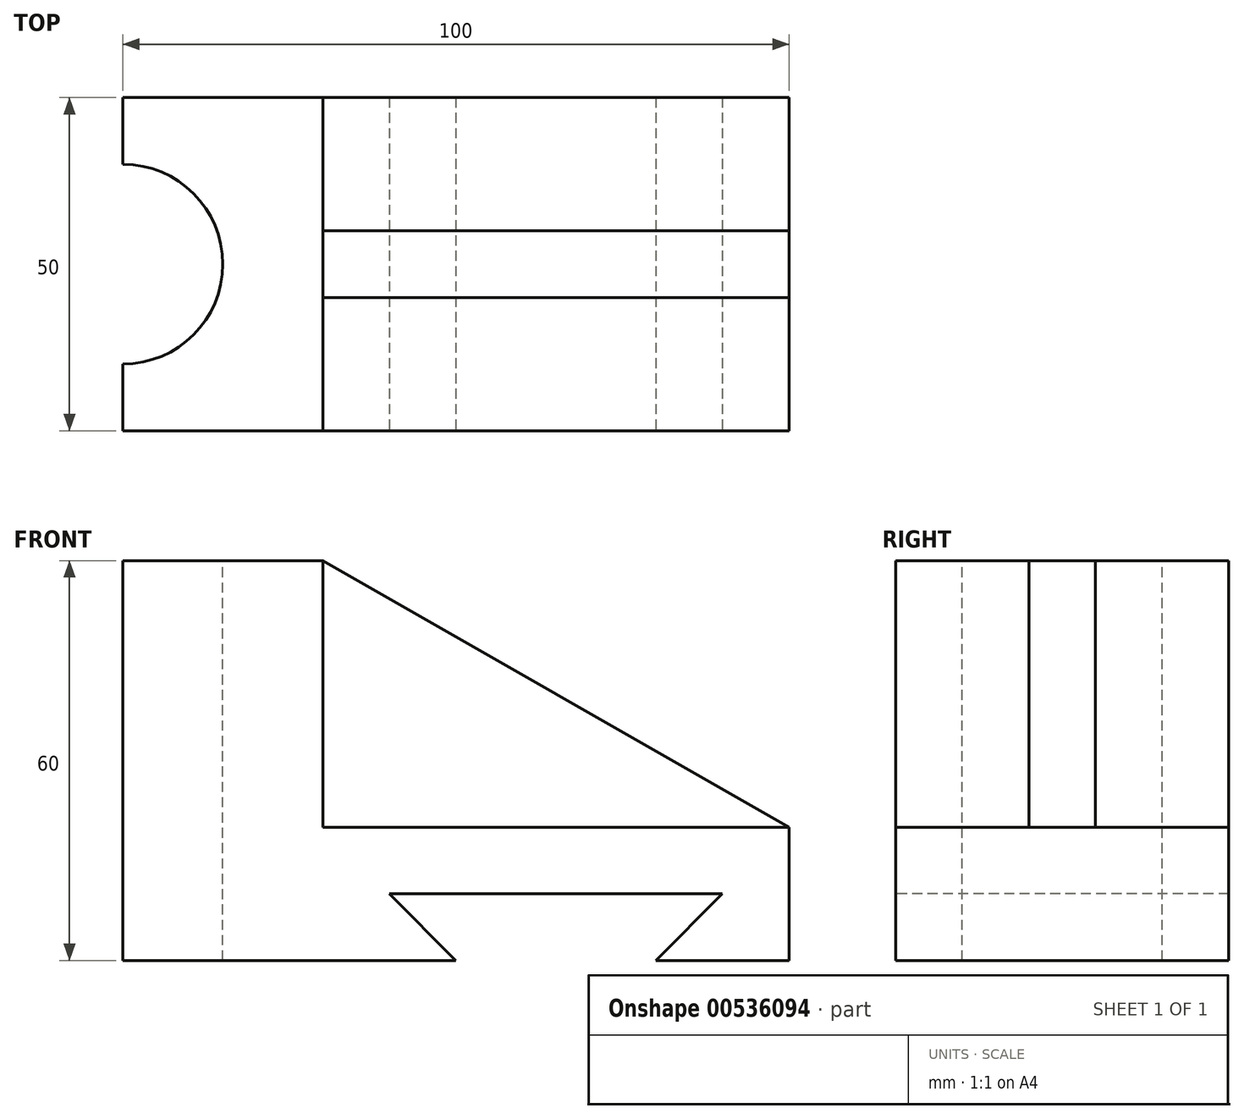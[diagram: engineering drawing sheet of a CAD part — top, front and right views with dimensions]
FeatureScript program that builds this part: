
annotation { "Feature Type Name" : "Feature", "Feature Type Description" : "" }
export const myFeature = defineFeature(function(context is Context, id is Id, definition is map)
    precondition{}
    {
        {
            var Q0;
            Q0=qCreatedBy(makeId("Top.planeOp"),FACE);
            var sketch = newSketch(context, id + "F0", { "sketchPlane" : qUnion([Q0])});
            skLineSegment(sketch, "E0.bottom", {"start": v(50, 25) * mm, "end": v(-50, 25) * mm});
            skLineSegment(sketch, "E0.top", {"start": v(50, -25) * mm, "end": v(-50, -25) * mm});
            skLineSegment(sketch, "E0.left", {"start": v(50, 25) * mm, "end": v(50, -25) * mm});
            skLineSegment(sketch, "E0.right", {"start": v(-50, 25) * mm, "end": v(-50, -25) * mm});
            skPoint(sketch, "E0.middle", {"position": v(0, 0) * mm});
            skLineSegment(sketch, "E1", {"start": v(-50, 25) * mm, "end": v(-20, 25) * mm});
            skLineSegment(sketch, "E2", {"start": v(-20, 25) * mm, "end": v(-20, -25) * mm});
            skLineSegment(sketch, "E3", {"start": v(-20, -25) * mm, "end": v(-50, -25) * mm});
            skSolve(sketch);
        }
        {
            var Q0;
            Q0=makeQuery(id+"F0.imprint","IMPRINT",FACE,{"disambiguationData":[TD([[makeQuery(id+"F0.imprint","IMPRINT",EDGE,{"derivedFrom":sQuery(id+"F0.wireOp",EDGE,"E0.right")}),1.0]])]});
            extrude(context, id + "F1", {"entities" : qUnion([Q0]), "depth" : 60 * mm, "offsetDistance" : 25 * mm});
        }
        {
            var Q0;
            Q0=makeQuery(id+"F0.imprint","IMPRINT",FACE,{"disambiguationData":[TD([[makeQuery(id+"F0.imprint","IMPRINT",EDGE,{"derivedFrom":sQuery(id+"F0.wireOp",EDGE,"E0.bottom")}),1.0]])]});
            extrude(context, id + "F2", {"entities" : qUnion([Q0]), "operationType" : NewBodyOperationType.ADD, "depth" : 20 * mm, "offsetDistance" : 25 * mm});
        }
        {
            var Q0;
            Q0=makeQuery(id+"F1.opExtrude","CAP_FACE",FACE,{"disambiguationData":[OSD([sQuery(id+"F0.wireOp",EDGE,"E0.right"),sQuery(id+"F0.wireOp",EDGE,"E1"),sQuery(id+"F0.wireOp",EDGE,"E2"),sQuery(id+"F0.wireOp",EDGE,"E3")])],"isStart":false});
            var sketch = newSketch(context, id + "F3", { "sketchPlane" : qUnion([Q0])});
            skPoint(sketch, "E4", {"position": v(-50, 15) * mm});
            skPoint(sketch, "E5", {"position": v(-50, -15) * mm});
            skCircle(sketch, "E6", {"center": v(-50, 0) * mm, "radius": 15 * mm});
            skSolve(sketch);
        }
        {
            var Q0;
            {var subQ0=sQuery(id+"F3.wireOp",EDGE,"E6");var subQ1=makeQuery(id+"F1.opExtrude","CAP_EDGE",EDGE,{"disambiguationData":[OSD([sQuery(id+"F0.wireOp",EDGE,"E0.right")])],"isStart":false});var subQ2=makeQuery(id+"F3.imprint","INTERSECT",VERTEX,{"disambiguationData":[OD(0.0)],"derivedFrom":[subQ1,subQ0]});Q0=makeQuery(id+"F3.imprint","IMPRINT",FACE,{"disambiguationData":[TD([[makeQuery(id+"F3.imprint","IMPRINT",EDGE,{"disambiguationData":[TD([[subQ2,1.0]])],"derivedFrom":subQ0}),1.0]])]});}
            extrude(context, id + "F4", {"entities" : qUnion([Q0]), "operationType" : NewBodyOperationType.REMOVE, "oppositeDirection" : true, "depth" : 71.1 * mm, "offsetDistance" : 25 * mm});
        }
        {
            var Q0;
            Q0=qCreatedBy(makeId("Front.planeOp"),FACE);
            var sketch = newSketch(context, id + "F5", { "sketchPlane" : qUnion([Q0])});
            skLineSegment(sketch, "E7.0.0", {"start": v(-50, 0) * mm, "end": v(50, 0) * mm});
            skLineSegment(sketch, "E7.0.1", {"start": v(50, 0) * mm, "end": v(50, 20) * mm});
            skLineSegment(sketch, "E7.0.2", {"start": v(50, 20) * mm, "end": v(-20, 20) * mm});
            skLineSegment(sketch, "E7.0.3", {"start": v(-20, 20) * mm, "end": v(-20, 60) * mm});
            skLineSegment(sketch, "E7.0.4", {"start": v(-20, 60) * mm, "end": v(-50, 60) * mm});
            skLineSegment(sketch, "E7.0.5", {"start": v(-50, 60) * mm, "end": v(-50, 0) * mm});
            skLineSegment(sketch, "E8", {"start": v(-20, 60) * mm, "end": v(50, 20) * mm});
            skSolve(sketch);
        }
        {
            var Q0;
            Q0=makeQuery(id+"F5.imprint","IMPRINT",FACE,{"disambiguationData":[TD([[makeQuery(id+"F5.imprint","IMPRINT",EDGE,{"derivedFrom":sQuery(id+"F5.wireOp",EDGE,"E7.0.2")}),-1.0]])]});
            extrude(context, id + "F6", {"entities" : qUnion([Q0]), "operationType" : NewBodyOperationType.ADD, "depth" : 5 * mm, "offsetDistance" : 25 * mm, "hasSecondDirection" : true, "secondDirectionOppositeDirection" : true, "secondDirectionDepth" : 5 * mm});
        }
        {
            var Q0;
            Q0=makeQuery(id+"F2.boolean.opBoolean","MERGE",FACE,{"derivedFrom":[makeQuery(id+"F1.opExtrude","SWEPT_FACE",FACE,{"disambiguationData":[OSD([sQuery(id+"F0.wireOp",EDGE,"E3")])]}),makeQuery(id+"F2.opExtrude","SWEPT_FACE",FACE,{"disambiguationData":[OSD([sQuery(id+"F0.wireOp",EDGE,"E0.top")])]})]});
            var sketch = newSketch(context, id + "F7", { "sketchPlane" : qUnion([Q0])});
            skLineSegment(sketch, "E9", {"start": v(50, 0) * mm, "end": v(30, 0) * mm});
            skLineSegment(sketch, "E10", {"start": v(30, 0) * mm, "end": v(0, 0) * mm});
            skLineSegment(sketch, "E11", {"start": v(0, 0) * mm, "end": v(-10, 10) * mm});
            skLineSegment(sketch, "E12", {"start": v(-10, 10) * mm, "end": v(40, 10) * mm});
            skLineSegment(sketch, "E13", {"start": v(40, 10) * mm, "end": v(30, 0) * mm});
            skSolve(sketch);
        }
        {
            var Q0;
            Q0=makeQuery(id+"F7.imprint","IMPRINT",FACE,{"disambiguationData":[TD([[makeQuery(id+"F7.imprint","IMPRINT",EDGE,{"derivedFrom":sQuery(id+"F7.wireOp",EDGE,"E10")}),-1.0]])]});
            extrude(context, id + "F8", {"entities" : qUnion([Q0]), "operationType" : NewBodyOperationType.REMOVE, "oppositeDirection" : true, "depth" : 205.9 * mm, "offsetDistance" : 25 * mm});
        }
    });
